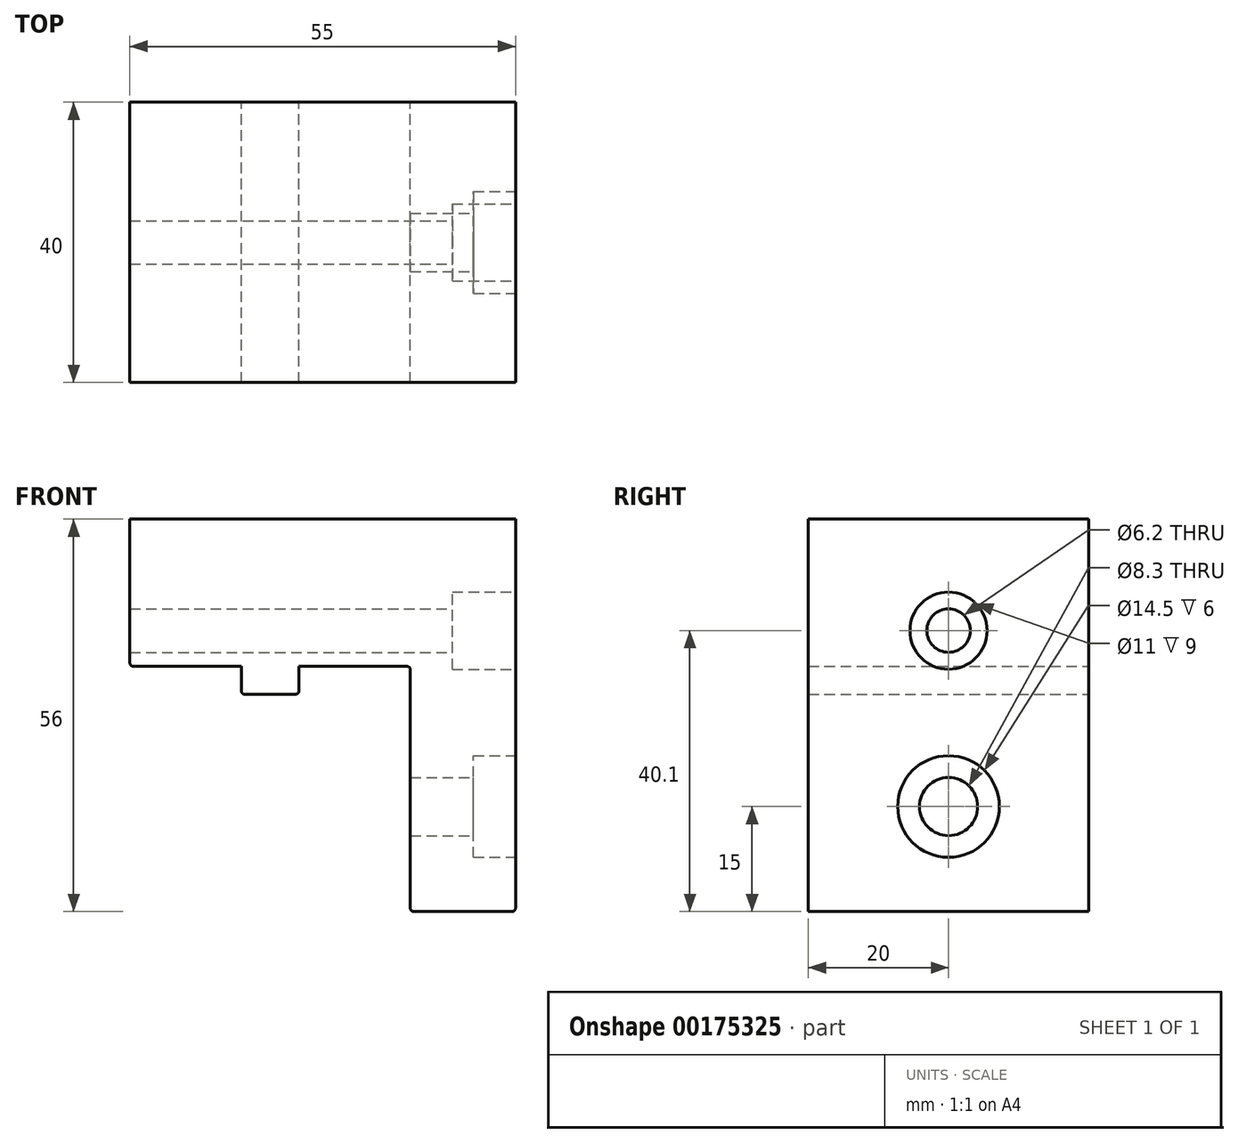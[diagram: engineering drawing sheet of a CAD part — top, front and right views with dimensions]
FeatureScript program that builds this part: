
annotation { "Feature Type Name" : "Feature", "Feature Type Description" : "" }
export const myFeature = defineFeature(function(context is Context, id is Id, definition is map)
    precondition{}
    {
        {
            var Q0;
            Q0=qCreatedBy(makeId("Front.planeOp"),FACE);
            var sketch = newSketch(context, id + "F0", { "sketchPlane" : qUnion([Q0])});
            skLineSegment(sketch, "E0", {"start": v(-20, 21) * mm, "end": v(-20, 0) * mm});
            skLineSegment(sketch, "E1", {"start": v(-20, 0) * mm, "end": v(-4.1, 0) * mm});
            skLineSegment(sketch, "E2", {"start": v(-4.1, 0) * mm, "end": v(-4.1, -4) * mm});
            skLineSegment(sketch, "E3", {"start": v(-4.1, -4) * mm, "end": v(4.1, -4) * mm});
            skLineSegment(sketch, "E4", {"start": v(4.1, -4) * mm, "end": v(4.1, 0) * mm});
            skLineSegment(sketch, "E5", {"start": v(4.1, 0) * mm, "end": v(20, 0) * mm});
            skLineSegment(sketch, "E6", {"start": v(35, 21) * mm, "end": v(-20, 21) * mm});
            skLineSegment(sketch, "E7", {"start": v(20, 0) * mm, "end": v(20, -35) * mm});
            skLineSegment(sketch, "E8", {"start": v(20, -35) * mm, "end": v(35, -35) * mm});
            skLineSegment(sketch, "E9", {"start": v(35, -35) * mm, "end": v(35, 21) * mm});
            skPoint(sketch, "E10", {"position": v(0, -4) * mm});
            skSolve(sketch);
        }
        {
            var Q0;
            Q0=makeQuery(id+"F0.imprint","IMPRINT",FACE,{"disambiguationData":[TD([[makeQuery(id+"F0.imprint","IMPRINT",EDGE,{"derivedFrom":sQuery(id+"F0.wireOp",EDGE,"E0")}),1.0]])]});
            extrude(context, id + "F1", {"entities" : qUnion([Q0]), "depth" : 40 * mm, "offsetDistance" : 25 * mm});
        }
        {
            var Q0;
            Q0=makeQuery(id+"F1.opExtrude","SWEPT_FACE",FACE,{"disambiguationData":[OSD([sQuery(id+"F0.wireOp",EDGE,"E9")])]});
            var sketch = newSketch(context, id + "F2", { "sketchPlane" : qUnion([Q0])});
            skCircle(sketch, "E11", {"center": v(-20, -20) * mm, "radius": 4.15 * mm});
            skPoint(sketch, "E11.centerSnap0", {"position": v(-20, -35) * mm});
            skCircle(sketch, "E12", {"center": v(-20, -20) * mm, "radius": 7.25 * mm});
            skCircle(sketch, "E13", {"center": v(-20, 5.1) * mm, "radius": 3.1 * mm});
            skPoint(sketch, "E13.centerSnap0", {"position": v(-20, 21) * mm});
            skCircle(sketch, "E14", {"center": v(-20, 5.1) * mm, "radius": 5.5 * mm});
            skSolve(sketch);
        }
        {
            var Q0;
            Q0=makeQuery(id+"F2.imprint","IMPRINT",FACE,{"disambiguationData":[TD([[makeQuery(id+"F2.imprint","IMPRINT",EDGE,{"derivedFrom":sQuery(id+"F2.wireOp",EDGE,"E11")}),1.0]])]});
            var Q1;
            Q1=makeQuery(id+"F2.imprint","IMPRINT",FACE,{"disambiguationData":[TD([[makeQuery(id+"F2.imprint","IMPRINT",EDGE,{"derivedFrom":sQuery(id+"F2.wireOp",EDGE,"E13")}),1.0]])]});
            extrude(context, id + "F3", {"entities" : qUnion([Q0, Q1]), "operationType" : NewBodyOperationType.REMOVE, "endBound" : BoundingType.UP_TO_NEXT, "oppositeDirection" : true, "depth" : 25 * mm, "offsetDistance" : 25 * mm});
        }
        {
            var Q0;
            Q0=makeQuery(id+"F1.opExtrude","SWEPT_EDGE",EDGE,{"disambiguationData":[OSD([sQuery(id+"F0.wireOp",EDGE,"E0"),sQuery(id+"F0.wireOp",EDGE,"E1")])]});
            var Q1;
            Q1=makeQuery(id+"F1.opExtrude","SWEPT_EDGE",EDGE,{"disambiguationData":[OSD([sQuery(id+"F0.wireOp",EDGE,"E2"),sQuery(id+"F0.wireOp",EDGE,"E3")])]});
            var Q2;
            Q2=makeQuery(id+"F1.opExtrude","SWEPT_EDGE",EDGE,{"disambiguationData":[OSD([sQuery(id+"F0.wireOp",EDGE,"E3"),sQuery(id+"F0.wireOp",EDGE,"E4")])]});
            var Q3;
            Q3=makeQuery(id+"F1.opExtrude","SWEPT_EDGE",EDGE,{"disambiguationData":[OSD([sQuery(id+"F0.wireOp",EDGE,"E5"),sQuery(id+"F0.wireOp",EDGE,"E7")])]});
            var Q4;
            Q4=makeQuery(id+"F1.opExtrude","SWEPT_EDGE",EDGE,{"disambiguationData":[OSD([sQuery(id+"F0.wireOp",EDGE,"E7"),sQuery(id+"F0.wireOp",EDGE,"E8")])]});
            var Q5;
            Q5=makeQuery(id+"F1.opExtrude","SWEPT_EDGE",EDGE,{"disambiguationData":[OSD([sQuery(id+"F0.wireOp",EDGE,"E8"),sQuery(id+"F0.wireOp",EDGE,"E9")])]});
            fillet(context, id + "F4", {"entities" : qUnion([Q0, Q1, Q2, Q3, Q4, Q5]), "tangentPropagation" : true, "radius" : 0.5 * mm, "defaultsChanged" : false, "vertexSettings" : [], "allowEdgeOverflow" : false});
        }
        {
            var Q0;
            Q0=makeQuery(id+"F2.imprint","IMPRINT",FACE,{"disambiguationData":[TD([[makeQuery(id+"F2.imprint","IMPRINT",EDGE,{"derivedFrom":sQuery(id+"F2.wireOp",EDGE,"E11")}),-1.0]])]});
            extrude(context, id + "F5", {"entities" : qUnion([Q0]), "operationType" : NewBodyOperationType.REMOVE, "oppositeDirection" : true, "depth" : 6 * mm, "offsetDistance" : 25 * mm});
        }
        {
            var Q0;
            Q0=makeQuery(id+"F2.imprint","IMPRINT",FACE,{"disambiguationData":[TD([[makeQuery(id+"F2.imprint","IMPRINT",EDGE,{"derivedFrom":sQuery(id+"F2.wireOp",EDGE,"E13")}),-1.0]])]});
            extrude(context, id + "F6", {"entities" : qUnion([Q0]), "operationType" : NewBodyOperationType.REMOVE, "oppositeDirection" : true, "depth" : 9 * mm, "offsetDistance" : 25 * mm});
        }
    });
